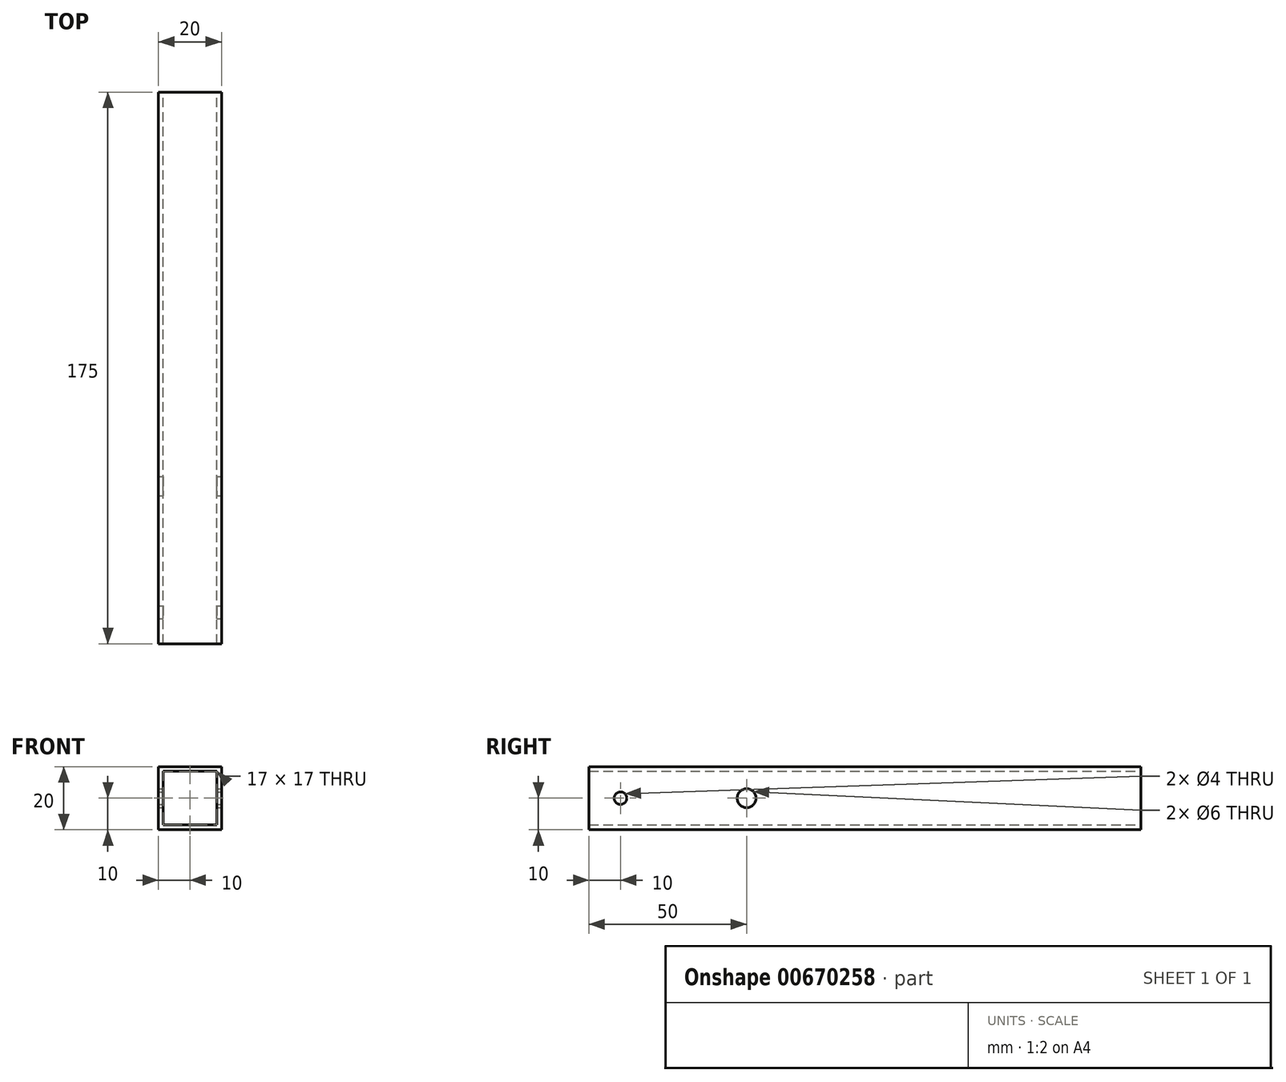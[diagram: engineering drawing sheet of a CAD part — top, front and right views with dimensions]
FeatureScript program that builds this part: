
annotation { "Feature Type Name" : "Feature", "Feature Type Description" : "" }
export const myFeature = defineFeature(function(context is Context, id is Id, definition is map)
    precondition{}
    {
        {
            var Q0;
            Q0=qCreatedBy(makeId("Front.planeOp"),FACE);
            var sketch = newSketch(context, id + "F0", { "sketchPlane" : qUnion([Q0])});
            skLineSegment(sketch, "E0.bottom", {"start": v(-10, 10) * mm, "end": v(10, 10) * mm});
            skLineSegment(sketch, "E0.top", {"start": v(-10, -10) * mm, "end": v(10, -10) * mm});
            skLineSegment(sketch, "E0.left", {"start": v(-10, 10) * mm, "end": v(-10, -10) * mm});
            skLineSegment(sketch, "E0.right", {"start": v(10, 10) * mm, "end": v(10, -10) * mm});
            skLineSegment(sketch, "E1.bottom", {"start": v(-8.5, 8.5) * mm, "end": v(8.5, 8.5) * mm});
            skLineSegment(sketch, "E1.top", {"start": v(-8.5, -8.5) * mm, "end": v(8.5, -8.5) * mm});
            skLineSegment(sketch, "E1.left", {"start": v(-8.5, 8.5) * mm, "end": v(-8.5, -8.5) * mm});
            skLineSegment(sketch, "E1.right", {"start": v(8.5, 8.5) * mm, "end": v(8.5, -8.5) * mm});
            skSolve(sketch);
        }
        {
            var Q0;
            Q0=qSketchRegion(id+"F0",true);
            extrude(context, id + "F1", {"entities" : qUnion([Q0]), "depth" : 175 * mm, "offsetDistance" : 25 * mm});
        }
        {
            var Q0;
            Q0=makeQuery(id+"F1.opExtrude","SWEPT_FACE",FACE,{"disambiguationData":[OSD([sQuery(id+"F0.wireOp",EDGE,"E0.right")])]});
            var sketch = newSketch(context, id + "F2", { "sketchPlane" : qUnion([Q0])});
            skPoint(sketch, "E2", {"position": v(-165, 0) * mm});
            skSolve(sketch);
        }
        {
            var Q0;
            Q0=sQuery(id+"F2.wireOp",VERTEX,"E2");
            var Q1;
            Q1=makeQuery(id+"F1.opExtrude","SWEPT_BODY",BODY,{"disambiguationData":[OSD([sQuery(id+"F0.wireOp",EDGE,"E0.bottom"),sQuery(id+"F0.wireOp",EDGE,"E0.top"),sQuery(id+"F0.wireOp",EDGE,"E0.left"),sQuery(id+"F0.wireOp",EDGE,"E0.right"),sQuery(id+"F0.wireOp",EDGE,"E1.bottom"),sQuery(id+"F0.wireOp",EDGE,"E1.top"),sQuery(id+"F0.wireOp",EDGE,"E1.left"),sQuery(id+"F0.wireOp",EDGE,"E1.right")])]});
            hole(context, id + "F3", {"style" : HoleStyle.SIMPLE, "endStyle" : HoleEndStyle.THROUGH, "holeDiameter" : 4 * mm, "majorDiameter" : 5 * mm, "isTappedThrough" : true, "tappedDepth" : 12 * mm, "tapClearance" : 3, "locations" : qUnion([Q0]), "scope" : qUnion([Q1])});
        }
        {
            var Q0;
            Q0=makeQuery(id+"F1.opExtrude","SWEPT_FACE",FACE,{"disambiguationData":[OSD([sQuery(id+"F0.wireOp",EDGE,"E0.right")])]});
            var sketch = newSketch(context, id + "F4", { "sketchPlane" : qUnion([Q0])});
            skPoint(sketch, "E3", {"position": v(-125, 0) * mm});
            skSolve(sketch);
        }
        {
            var Q0;
            Q0=sQuery(id+"F4.wireOp",VERTEX,"E3");
            var Q1;
            Q1=makeQuery(id+"F1.opExtrude","SWEPT_BODY",BODY,{"disambiguationData":[OSD([sQuery(id+"F0.wireOp",EDGE,"E0.bottom"),sQuery(id+"F0.wireOp",EDGE,"E0.top"),sQuery(id+"F0.wireOp",EDGE,"E0.left"),sQuery(id+"F0.wireOp",EDGE,"E0.right"),sQuery(id+"F0.wireOp",EDGE,"E1.bottom"),sQuery(id+"F0.wireOp",EDGE,"E1.top"),sQuery(id+"F0.wireOp",EDGE,"E1.left"),sQuery(id+"F0.wireOp",EDGE,"E1.right")])]});
            hole(context, id + "F5", {"style" : HoleStyle.SIMPLE, "endStyle" : HoleEndStyle.THROUGH, "holeDiameter" : 6 * mm, "majorDiameter" : 5 * mm, "isTappedThrough" : true, "tappedDepth" : 12 * mm, "tapClearance" : 3, "locations" : qUnion([Q0]), "scope" : qUnion([Q1])});
        }
    });
